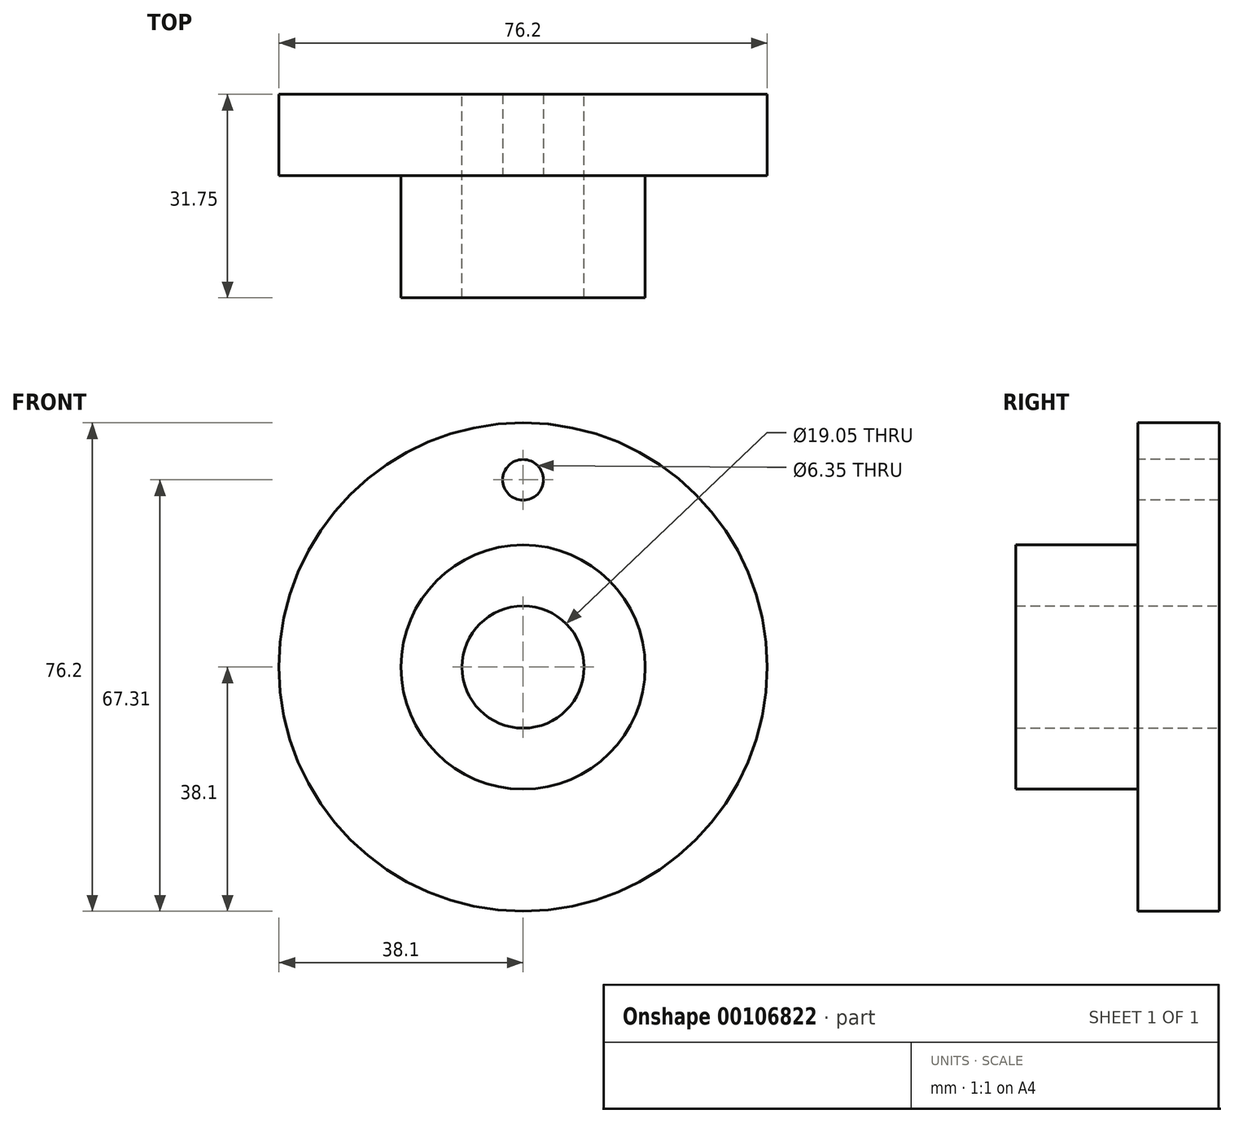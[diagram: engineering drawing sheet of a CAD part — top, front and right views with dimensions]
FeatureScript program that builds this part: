
annotation { "Feature Type Name" : "Feature", "Feature Type Description" : "" }
export const myFeature = defineFeature(function(context is Context, id is Id, definition is map)
    precondition{}
    {
        {
            var Q0;
            Q0=qCreatedBy(makeId("Front.planeOp"),FACE);
            var sketch = newSketch(context, id + "F0", { "sketchPlane" : qUnion([Q0])});
            skCircle(sketch, "E0", {"center": v(0, 0) * mm, "radius": 38.1 * mm});
            skCircle(sketch, "E1", {"center": v(0, 0) * mm, "radius": 19.05 * mm});
            skCircle(sketch, "E2", {"center": v(0, 0) * mm, "radius": 9.53 * mm});
            skSolve(sketch);
        }
        {
            var Q0;
            Q0 = qSketchRegion(id + "F0", true);
            extrude(context, id + "F1", {"entities" : qUnion([Q0]), "depth" : 12.7 * mm});
        }
        {
            var Q0;
            Q0=makeQuery(id+"F0.imprint","IMPRINT",FACE,{"disambiguationData":[TD([[makeQuery(id+"F0.imprint","IMPRINT",EDGE,{"derivedFrom":sQuery(id+"F0.wireOp",EDGE,"E1")}),1.0]])]});
            extrude(context, id + "F2", {"entities" : qUnion([Q0]), "operationType" : NewBodyOperationType.ADD, "depth" : 31.75 * mm});
        }
        {
            var Q0;
            Q0=makeQuery(id+"F1.opExtrude","CAP_FACE",FACE,{"disambiguationData":[OSD([sQuery(id+"F0.wireOp",EDGE,"E0"),sQuery(id+"F0.wireOp",EDGE,"E1")])],"isStart":false});
            var sketch = newSketch(context, id + "F3", { "sketchPlane" : qUnion([Q0])});
            skCircle(sketch, "E3", {"center": v(0, 29.21) * mm, "radius": 3.18 * mm});
            skSolve(sketch);
        }
        {
            var Q0;
            Q0=makeQuery(id+"F3.imprint","IMPRINT",FACE,{"disambiguationData":[TD([[makeQuery(id+"F3.imprint","IMPRINT",EDGE,{"derivedFrom":sQuery(id+"F3.wireOp",EDGE,"E3")}),1.0]])]});
            var Q1;
            Q1=sQuery(id+"F3.wireOp",EDGE,"E3");
            extrude(context, id + "F4", {"entities" : qUnion([Q0]), "operationType" : NewBodyOperationType.REMOVE, "surfaceEntities" : qUnion([Q1]), "endBound" : BoundingType.THROUGH_ALL, "oppositeDirection" : true, "depth" : 25.4 * mm});
        }
    });
